# Revit family: Artemide_Discovery_Space
name_source: partatom
category: Lighting Fixtures
revit_build: Autodesk Revit 2018 (Build: 20190510_1515(x64)
units: mm (PartAtom-declared; Revit-internal decimal feet)

## family parameters
Always vertical = Yes
Cut with Voids When Loaded = No
Light Source = No
Part Type = Normal
Room Calculation Point = No
Round Connector Dimension = Use Diameter
Shared = No
Work Plane-Based = Yes

## types (36) — shared parameters
6 Monthly = -
Air Handling = -
Angle_A_Max = 90.00°
Angle_A_Min = 0.00°
Angle_B_Max = 180.00°
Angle_B_Min = 90.00°
Annually = -
Application Environment = Internal
Beam Angle Longditudinal Axis  = 0.00°
Beam Angle Transverse Axis  = 0.00°
Bespoke Timeframe = -
CE Approval = Y
Cable Material = -
Column = -
Control Gear Location = -
Control Gear Required = -
Control Gear Type = -
Daily = -
Daylight Sensor = -
Default Elevation = 1219 mm
Diffuser Finish = -
Diffuser Material  = -
Diffusing screen = -
Earth Point  = -
Emergency = N
Emergency Lighting Battery = -
End Caps/Transition Caps/Joints = -
Environmental Product Declaration = -
Expected Life = -
Features = -
Fire Rated = -
Fire Shroud = -
Fixing Material = -
Fixings = Y
Gasket Material = -
Green Guide for Specification = -
Hazardous Area Category = -
Hazardous Area Protection Type = -
Housing Material = Aluminum
IK Rating = -
IP Rating = IP20
IfcExportAs = IfcLightFixtureType
IfcExportType = NOT DEFINED
Infills = -
Integral Emergency Lighting Battery Type = -
Integral Fuse or Circuit Protection  = -
Intended Market = Unset
International Type Code = -
LED lifetime = 50000
Lamp Cap = LED Integrated
Lamp Holder Material = -
Lamp Included = Y
Lamp Replacement Interval = -
Lamp Survival Factor = -
Life Cycle Analysis = -
Light Fixture Mounting Type = Suspended
Light Output Pattern = -
Location of Manufacturer = -
Louvre/Lens = -
Luminaire Cleaning Interval  = -
Luminaire Type = Unset
M_Cable = Artemide_Aluminum_Anodized
Maintenance Required: 0-300hrs  = -
Maintenance Required: 1001-2000hrs  = -
Maintenance Required: 2001-4000hrs  = -
Maintenance Required: 301-600hrs  = -
Maintenance Required: 4001-8000hrs  = -
Maintenance Required: 601-1000hrs = -
Maintenance Required: 8001-12000hrs  = -
Manufacturer = Artemide
Manufacturer Website = https://www.artemide.com
Material Ingredient Reporting = -
Monthly = -
Motion Detector = -
Motion Sensor = -
Number of Primary Lamps = 1
Overall Width = 17
Photocell = -
Power Supply Kit = -
Product Literature = https://www.artemide.com
Product Range = Discovery
Quarterly = -
Rated Lamp Life = 50000
Reflector Finish = -
Reflector Material = Technopolymer
Responsible Extraction of Materials = -
Responsible Sourcing of Materials = -
Secondary Lamp = N
Secondary Lamp Cap = -
Secondary Lamp Included = -
Secondary Lamp International Type Code = -
Service life  = -
Standards = -
Suitable for Dimming  = Y
Suitable for Motion Detector Control = N
Suitable for Photocell Control = -
Testing method = -
Trim Colour  = -
Trim Finish = -
Trim Material = -
URL to Energy Technology List = -
URL to O&M Manual = -
Uniclass 2015 = Pr_70_70_48
Unified Glare Rating  = -
Voltage = -
Warranty ID = https://cloud.artemide.com
Weekly = -
zero-valued in all types: A, Access Clearance Bottom, Access Clearance Front, Access Clearance Left, Access Clearance Rear, Access Clearance Right, Access Clearance Top, Ambient Temperature                            , Basis of lifetime lumen depreciation  , Basis of lifetime luminaire failures       , Control Gear Standby Power , Current , Cut Out Length, Cut Out Width, Downward Component, Drive Current                                         , Duration of Integral Emergency Lighting , Embodied Carbon , Emergency Charging Power      , Emergency light output percentage, External Control Line Voltage, Face Length, Face Width, Fire Rated Temperature, Fire Rating Duration, Frequency , Input Lumens Indirect light, LED Initial Colour Variation                     , LED Maintained Colour Variation        , Luminaire Maintenance Factor, Luminance at 65deg Angle, Max Height from ceiling, Maximum Operating Temperature, Minimum Operating Temperature, Number of Poles, Number of Secondary Lamps, Output Lumens Indirect light, Overall Light Output Ratio, Power Factor, Secondary Lamp Colour Rendering Index, Secondary Lamp Colour Temperature, Secondary Lamp Efficacy, Secondary Lamp Initial Lumens , Secondary Lamp Voltage, Secondary Rated Lamp Life, Shipping Weight, Supply Phase, Total Light Output , Total Power, Upward Component 

## per-type parameters (varying)
| type | Colour Rendering Index | Colour Temperature | ENEC Certification of European conformity | Efficiency | Face Shape | Gross Weight | Housing Colour  | Housing Finish  | IES Files  | Initial Lumens | Input Lumens Direct light | Length_SideA | Length_SideB | M_Diffuser | M_Housing | Output Lumens Direct light | Overall Height | Overall Length | Primary Lamp Type | Product Model Number | Suitable Dimmer Type | TypeSelector |
| Discovery_Space_Square_SatinizedAluminum_2004010A | 90 | 3000 | Y | 41 | Square | 7.7 | Aluminum | Satinized | https://www.artemide.com | 1955 | 1955.25 | 900 mm  [stored 2.95276 ft] | 900 mm  [stored 2.95276 ft] | Artemide_Glass_LightBulb | Artemide_Aluminum_Satinized | 1955 | 900 | 900 | LED | 2004010A | Push/DALI | Artemide_Discovery_Space_AngleA+AngleB : Discovery_Space_Square_SatinizedAluminum_2004010A |
| Discovery_Space_Rectangular_SatinizedAluminum_2005010A | 90 | 3000 | Y | 55 | Rectangular | 8.7 | Aluminum | Satinized | https://www.artemide.com | 4002 | 4002.42 | 1540 mm  [stored 5.05249 ft] | 770 mm  [stored 2.52625 ft] | Artemide_Glass_LightBulb | Artemide_Aluminum_Satinized | 4002 | 1540 | 770 | LED | 2005010A | Push/DALI | Artemide_Discovery_Space_AngleA+AngleB : Discovery_Space_Rectangular_SatinizedAluminum_2005010A |
| Discovery_Space_Square_Black_2004030A | 90 | 3000 | Y | 41 | Square | 7.7 | Black | Painted | https://www.artemide.com | 1955 | 1955.25 | 900 mm  [stored 2.95276 ft] | 900 mm  [stored 2.95276 ft] | Artemide_Glass_LightBulb | Artemide_Aluminum_Black | 1955 | 900 | 900 | LED | 2004030A | Push/DALI | Artemide_Discovery_Space_AngleA+AngleB : Discovery_Space_Square_Black_2004030A |
| Discovery_Space_Square_Bronze_2004060A | 90 | 3000 | Y | 41 | Square | 7.7 | Bronze | Painted | https://www.artemide.com | 1955 | 1955.25 | 900 mm  [stored 2.95276 ft] | 900 mm  [stored 2.95276 ft] | Artemide_Glass_LightBulb | Artemide_Aluminum_Bronze | 1955 | 900 | 900 | LED | 2004060A | Push/DALI | Artemide_Discovery_Space_AngleA+AngleB : Discovery_Space_Square_Bronze_2004060A |
| Discovery_Space_Square_SatinizedAluminum_APPCompatible_2004010APP | 90 | 3000 | Y | 41 | Square | 7.7 | Aluminum | Satinized | - | 1955 | 1955.25 | 900 mm  [stored 2.95276 ft] | 900 mm  [stored 2.95276 ft] | Artemide_Glass_LightBulb | Artemide_Aluminum_Satinized | 1955 | 900 | 900 | LED | 2004010APP | Push & APP | Artemide_Discovery_Space_AngleA+AngleB : Discovery_Space_Square_SatinizedAluminum_APPCompatible_2004010APP |
| Discovery_Space_Square_Black_APPCompatible_2004030APP | 90 | 3000 | Y | 41 | Square | 7.7 | Black | Painted | https://www.artemide.com | 1955 | 1955.25 | 900 mm  [stored 2.95276 ft] | 900 mm  [stored 2.95276 ft] | Artemide_Glass_LightBulb | Artemide_Aluminum_Black | 1955 | 900 | 900 | LED | 2004030APP | Push & APP | Artemide_Discovery_Space_AngleA+AngleB : Discovery_Space_Square_Black_APPCompatible_2004030APP |
| Discovery_Space_Square_Bronze_APPCompatible_2004060APP | 90 | 3000 | Y | 41 | Square | 7.7 | Bronze | Painted | https://www.artemide.com | 1955 | 1955.25 | 900 mm  [stored 2.95276 ft] | 900 mm  [stored 2.95276 ft] | Artemide_Glass_LightBulb | Artemide_Aluminum_Bronze | 1955 | 900 | 900 | LED | 2004060APP | Push & APP | Artemide_Discovery_Space_AngleA+AngleB : Discovery_Space_Square_Bronze_APPCompatible_2004060APP |
| Discovery_Space_Square_TW_SatinizedAluminum_2000010A | 0 | 0 | N | 100 | Square | 7.7 | Aluminum | Satinized | - | 0 | 0 | 900 mm  [stored 2.95276 ft] | 900 mm  [stored 2.95276 ft] | Artemide_Glass_LightBulb | Artemide_Aluminum_Satinized | 0 | 900 | 900 | LED TW | 2000010A | Dali | Artemide_Discovery_Space_AngleA+AngleB : Discovery_Space_Square_TW_SatinizedAluminum_2000010A |
| Discovery_Space_Square_TW_Black_2000030A | 0 | 0 | N | 100 | Square | 7.7 | Black | Painted | - | 0 | 0 | 900 mm  [stored 2.95276 ft] | 900 mm  [stored 2.95276 ft] | Artemide_Glass_LightBulb | Artemide_Aluminum_Black | 0 | 900 | 900 | LED TW | 2000030A | Dali | Artemide_Discovery_Space_AngleA+AngleB : Discovery_Space_Square_TW_Black_2000030A |
| Discovery_Space_Square_TW_Bronze_2000060A | 0 | 0 | N | 100 | Square | 7.7 | Bronze | Painted | - | 0 | 0 | 900 mm  [stored 2.95276 ft] | 900 mm  [stored 2.95276 ft] | Artemide_Glass_LightBulb | Artemide_Aluminum_Bronze | 0 | 900 | 900 | LED TW | 2000060A | Dali | Artemide_Discovery_Space_AngleA+AngleB : Discovery_Space_Square_TW_Bronze_2000060A |
| Discovery_Space_Square_TW_SatinizedAluminum_APPCompatible_2000010APP | 0 | 0 | N | 100 | Square | 7.7 | Aluminum | Satinized | - | 0 | 0 | 900 mm  [stored 2.95276 ft] | 900 mm  [stored 2.95276 ft] | Artemide_Glass_LightBulb | Artemide_Aluminum_Satinized | 0 | 900 | 900 | LED TW | 2000010APP | APP | Artemide_Discovery_Space_AngleA+AngleB : Discovery_Space_Square_TW_SatinizedAluminum_APPCompatible_2000010APP |
| Discovery_Space_Square_TW_Black_APPCompatible_2000030APP | 0 | 0 | N | 100 | Square | 7.7 | Black | Painted | - | 0 | 0 | 900 mm  [stored 2.95276 ft] | 900 mm  [stored 2.95276 ft] | Artemide_Glass_LightBulb | Artemide_Aluminum_Black | 0 | 900 | 900 | LED TW | 2000030APP | APP | Artemide_Discovery_Space_AngleA+AngleB : Discovery_Space_Square_TW_Black_APPCompatible_2000030APP |
| Discovery_Space_Square_TW_Bronze_APPCompatible_2000060APP | 0 | 0 | N | 100 | Square | 7.7 | Bronze | Painted | - | 0 | 0 | 900 mm  [stored 2.95276 ft] | 900 mm  [stored 2.95276 ft] | Artemide_Glass_LightBulb | Artemide_Aluminum_Bronze | 0 | 900 | 900 | LED TW | 2000060APP | APP | Artemide_Discovery_Space_AngleA+AngleB : Discovery_Space_Square_TW_Bronze_APPCompatible_2000060APP |
| Discovery_Space_Square_RGBW_SatinizedAluminum_2001010A | 0 | 0 | N | 96 | Square | 7.7 | Aluminum | Satinized | - | 1637 | 0 | 900 mm  [stored 2.95276 ft] | 900 mm  [stored 2.95276 ft] | Artemide_Glass_LightBulbRGB | Artemide_Aluminum_Satinized | 1637 | 900 | 900 | LED RGBW | 2001010A | Dali | Artemide_Discovery_Space_AngleA+AngleB : Discovery_Space_Square_RGBW_SatinizedAluminum_2001010A |
| Discovery_Space_Square_RGBW_Black_2001030A | 0 | 0 | N | 96 | Square | 7.7 | Black | Painted | - | 1637 | 0 | 900 mm  [stored 2.95276 ft] | 900 mm  [stored 2.95276 ft] | Artemide_Glass_LightBulbRGB | Artemide_Aluminum_Black | 1637 | 900 | 900 | LED RGBW | 2001030A | Dali | Artemide_Discovery_Space_AngleA+AngleB : Discovery_Space_Square_RGBW_Black_2001030A |
| Discovery_Space_Square_RGBW_Bronze_2001060A | 0 | 0 | N | 96 | Square | 7.7 | Bronze | Painted | - | 1637 | 0 | 900 mm  [stored 2.95276 ft] | 900 mm  [stored 2.95276 ft] | Artemide_Glass_LightBulbRGB | Artemide_Aluminum_Bronze | 1637 | 900 | 900 | LED RGBW | 2001060A | Dali | Artemide_Discovery_Space_AngleA+AngleB : Discovery_Space_Square_RGBW_Bronze_2001060A |
| Discovery_Space_Square_RGBW_SatinizedAluminum_APPCompatible_2001010APP | 0 | 0 | N | 96 | Square | 7.7 | Aluminum | Satinized | - | 1637 | 0 | 900 mm  [stored 2.95276 ft] | 900 mm  [stored 2.95276 ft] | Artemide_Glass_LightBulbRGB | Artemide_Aluminum_Satinized | 1637 | 900 | 900 | LED RGBW | 2001010APP | APP | Artemide_Discovery_Space_AngleA+AngleB : Discovery_Space_Square_RGBW_SatinizedAluminum_APPCompatible_2001010APP |
| Discovery_Space_Square_RGBW_Black_APPCompatible_2001030APP | 0 | 0 | N | 96 | Square | 7.7 | Black | Painted | - | 1637 | 0 | 900 mm  [stored 2.95276 ft] | 900 mm  [stored 2.95276 ft] | Artemide_Glass_LightBulbRGB | Artemide_Aluminum_Black | 1637 | 900 | 900 | LED RGBW | 2001030APP | APP | Artemide_Discovery_Space_AngleA+AngleB : Discovery_Space_Square_RGBW_Black_APPCompatible_2001030APP |
| Discovery_Space_Square_RGBW_Bronze_APPCompatible_2001060APP | 0 | 0 | N | 96 | Square | 7.7 | Bronze | Painted | - | 1637 | 0 | 900 mm  [stored 2.95276 ft] | 900 mm  [stored 2.95276 ft] | Artemide_Glass_LightBulbRGB | Artemide_Aluminum_Bronze | 1637 | 900 | 900 | LED RGBW | 2001060APP | APP | Artemide_Discovery_Space_AngleA+AngleB : Discovery_Space_Square_RGBW_Bronze_APPCompatible_2001060APP |
| Discovery_Space_Rectangular_Black_2005030A | 90 | 3000 | Y | 55 | Rectangular | 8.7 | Black | Painted | https://www.artemide.com | 4002 | 4002.42 | 1540 mm  [stored 5.05249 ft] | 770 mm  [stored 2.52625 ft] | Artemide_Glass_LightBulb | Artemide_Aluminum_Black | 4002 | 1540 | 770 | LED | 2005030A | Push/DALI | Artemide_Discovery_Space_AngleA+AngleB : Discovery_Space_Rectangular_Black_2005030A |
| Discovery_Space_Rectangular_Bronze_2005060A | 90 | 3000 | Y | 55 | Rectangular | 8.7 | Bronze | Painted | https://www.artemide.com | 4002 | 4002.42 | 1540 mm  [stored 5.05249 ft] | 770 mm  [stored 2.52625 ft] | Artemide_Glass_LightBulb | Artemide_Aluminum_Bronze | 4002 | 1540 | 770 | LED | 2005060A | Push/DALI | Artemide_Discovery_Space_AngleA+AngleB : Discovery_Space_Rectangular_Bronze_2005060A |
| Discovery_Space_Rectangular_SatinizedAluminum_APPCompatible_2005010APP | 90 | 3000 | Y | 55 | Rectangular | 8.7 | Aluminum | Satinized | https://www.artemide.com | 4002 | 4002.42 | 1540 mm  [stored 5.05249 ft] | 770 mm  [stored 2.52625 ft] | Artemide_Glass_LightBulb | Artemide_Aluminum_Satinized | 4002 | 1540 | 770 | LED | 2005010APP | Push & APP | Artemide_Discovery_Space_AngleA+AngleB : Discovery_Space_Rectangular_SatinizedAluminum_APPCompatible_2005010APP |
| Discovery_Space_Rectangular_Black_APPCompatible_2005030APP | 90 | 3000 | Y | 55 | Rectangular | 8.7 | Black | Painted | https://www.artemide.com | 4002 | 4002.42 | 1540 mm  [stored 5.05249 ft] | 770 mm  [stored 2.52625 ft] | Artemide_Glass_LightBulb | Artemide_Aluminum_Black | 4002 | 1540 | 770 | LED | 2005030APP | Push & APP | Artemide_Discovery_Space_AngleA+AngleB : Discovery_Space_Rectangular_Black_APPCompatible_2005030APP |
| Discovery_Space_Rectangular_Bronze_APPCompatible_2005060APP | 90 | 3000 | Y | 55 | Rectangular | 8.7 | Bronze | Painted | https://www.artemide.com | 4002 | 4002.42 | 1540 mm  [stored 5.05249 ft] | 770 mm  [stored 2.52625 ft] | Artemide_Glass_LightBulb | Artemide_Aluminum_Bronze | 4002 | 1540 | 770 | LED | 2005060APP | Push & APP | Artemide_Discovery_Space_AngleA+AngleB : Discovery_Space_Rectangular_Bronze_APPCompatible_2005060APP |
| Discovery_Space_Rectangular_TW_SatinizedAluminum_2002010A | 80 | 0 | N | 100 | Rectangular | 8.7 | Aluminum | Satinized | - | 0 | 0 | 1540 mm  [stored 5.05249 ft] | 770 mm  [stored 2.52625 ft] | Artemide_Glass_LightBulb | Artemide_Aluminum_Satinized | 0 | 1540 | 770 | LED TW | 2002010A | Dali | Artemide_Discovery_Space_AngleA+AngleB : Discovery_Space_Rectangular_TW_SatinizedAluminum_2002010A |
| Discovery_Space_Rectangular_TW_Black_2002030A | 80 | 0 | N | 100 | Rectangular | 8.7 | Black | Painted | - | 0 | 0 | 1540 mm  [stored 5.05249 ft] | 770 mm  [stored 2.52625 ft] | Artemide_Glass_LightBulb | Artemide_Aluminum_Black | 0 | 1540 | 770 | LED TW | 2002030A | Dali | Artemide_Discovery_Space_AngleA+AngleB : Discovery_Space_Rectangular_TW_Black_2002030A |
| Discovery_Space_Rectangular_TW_Bronze_2002060A | 80 | 0 | N | 100 | Rectangular | 8.7 | Bronze | Painted | - | 0 | 0 | 1540 mm  [stored 5.05249 ft] | 770 mm  [stored 2.52625 ft] | Artemide_Glass_LightBulb | Artemide_Aluminum_Bronze | 0 | 1540 | 770 | LED TW | 2002060A | Dali | Artemide_Discovery_Space_AngleA+AngleB : Discovery_Space_Rectangular_TW_Bronze_2002060A |
| Discovery_Space_Rectangular_TW_SatinizedAluminum_APPCompatible_2002010APP | 80 | 0 | N | 100 | Rectangular | 8.7 | Aluminum | Satinized | - | 0 | 0 | 1540 mm  [stored 5.05249 ft] | 770 mm  [stored 2.52625 ft] | Artemide_Glass_LightBulb | Artemide_Aluminum_Satinized | 0 | 1540 | 770 | LED TW | 2002010APP | APP | Artemide_Discovery_Space_AngleA+AngleB : Discovery_Space_Rectangular_TW_SatinizedAluminum_APPCompatible_2002010APP |
| Discovery_Space_Rectangular_TW_Black_APPCompatible_2002030APP | 80 | 0 | N | 100 | Rectangular | 8.7 | Black | Painted | - | 0 | 0 | 1540 mm  [stored 5.05249 ft] | 770 mm  [stored 2.52625 ft] | Artemide_Glass_LightBulb | Artemide_Aluminum_Black | 0 | 1540 | 770 | LED TW | 2002030APP | APP | Artemide_Discovery_Space_AngleA+AngleB : Discovery_Space_Rectangular_TW_Black_APPCompatible_2002030APP |
| Discovery_Space_Rectangular_TW_Bronze_APPCompatible_2002060APP | 80 | 0 | N | 100 | Rectangular | 8.7 | Bronze | Painted | - | 0 | 0 | 1540 mm  [stored 5.05249 ft] | 770 mm  [stored 2.52625 ft] | Artemide_Glass_LightBulb | Artemide_Aluminum_Bronze | 0 | 1540 | 770 | LED TW | 2002060APP | APP | Artemide_Discovery_Space_AngleA+AngleB : Discovery_Space_Rectangular_TW_Black_APPCompatible_2002030APP |
| Discovery_Space_Rectangular_RGBW_SatinizedAluminum_2003010A | 0 | 0 | N | 100 | Rectangular | 8.7 | Aluminum | Satinized | - | 2664 | 0 | 1540 mm  [stored 5.05249 ft] | 770 mm  [stored 2.52625 ft] | Artemide_Glass_LightBulbRGB | Artemide_Aluminum_Satinized | 2664 | 1540 | 770 | LED RGBW | 2003010A | Dali | Artemide_Discovery_Space_AngleA+AngleB : Discovery_Space_Rectangular_RGBW_SatinizedAluminum_2003010A |
| Discovery_Space_Rectangular_RGBW_Black_2003030A | 0 | 0 | N | 100 | Rectangular | 8.7 | Black | Painted | - | 2664 | 0 | 1540 mm  [stored 5.05249 ft] | 770 mm  [stored 2.52625 ft] | Artemide_Glass_LightBulbRGB | Artemide_Aluminum_Black | 2664 | 1540 | 770 | LED RGBW | 2003030A | Dali | Artemide_Discovery_Space_AngleA+AngleB : Discovery_Space_Rectangular_RGBW_Black_2003030A |
| Discovery_Space_Rectangular_RGBW_Bronze_2003060A | 0 | 0 | N | 100 | Rectangular | 8.7 | Bronze | Painted | - | 2664 | 0 | 1540 mm  [stored 5.05249 ft] | 770 mm  [stored 2.52625 ft] | Artemide_Glass_LightBulbRGB | Artemide_Aluminum_Bronze | 2664 | 1540 | 770 | LED RGBW | 2003060A | Dali | Artemide_Discovery_Space_AngleA+AngleB : Discovery_Space_Rectangular_RGBW_Bronze_2003060A |
| Discovery_Space_Rectangular_RGBW_SatinizedAluminum_APPCompatible_2003010APP | 0 | 0 | N | 100 | Rectangular | 8.7 | Aluminum | Satinized | - | 2664 | 0 | 1540 mm  [stored 5.05249 ft] | 770 mm  [stored 2.52625 ft] | Artemide_Glass_LightBulbRGB | Artemide_Aluminum_Satinized | 2664 | 1540 | 770 | LED RGBW | 2003010APP | APP | Artemide_Discovery_Space_AngleA+AngleB : Discovery_Space_Rectangular_RGBW_SatinizedAluminum_APPCompatible_2003010APP |
| Discovery_Space_Rectangular_RGBW_Black_APPCompatible_2003030APP | 0 | 0 | N | 100 | Rectangular | 8.7 | Black | Painted | - | 2664 | 0 | 1540 mm  [stored 5.05249 ft] | 770 mm  [stored 2.52625 ft] | Artemide_Glass_LightBulbRGB | Artemide_Aluminum_Black | 2664 | 1540 | 770 | LED RGBW | 2003030APP | APP | Artemide_Discovery_Space_AngleA+AngleB : Discovery_Space_Rectangular_RGBW_Black_APPCompatible_2003030APP |
| Discovery_Space_Rectangular_RGBW_Bronze_APPCompatible_2003060APP | 0 | 0 | N | 100 | Rectangular | 8.7 | Bronze | Painted | - | 2664 | 0 | 1540 mm  [stored 5.05249 ft] | 770 mm  [stored 2.52625 ft] | Artemide_Glass_LightBulbRGB | Artemide_Aluminum_Bronze | 2664 | 1540 | 770 | LED RGBW | 2003060APP | APP | Artemide_Discovery_Space_AngleA+AngleB : Discovery_Space_Rectangular_RGBW_Bronze_APPCompatible_2003060APP |

note: [stored X ft] marks values corroborated as IEEE doubles in the binary element streams (Revit-internal decimal feet)

## geometry (parser evidence)
native form markers: Blend x2, Sweep x17
no freeform markers — native parametric forms only
